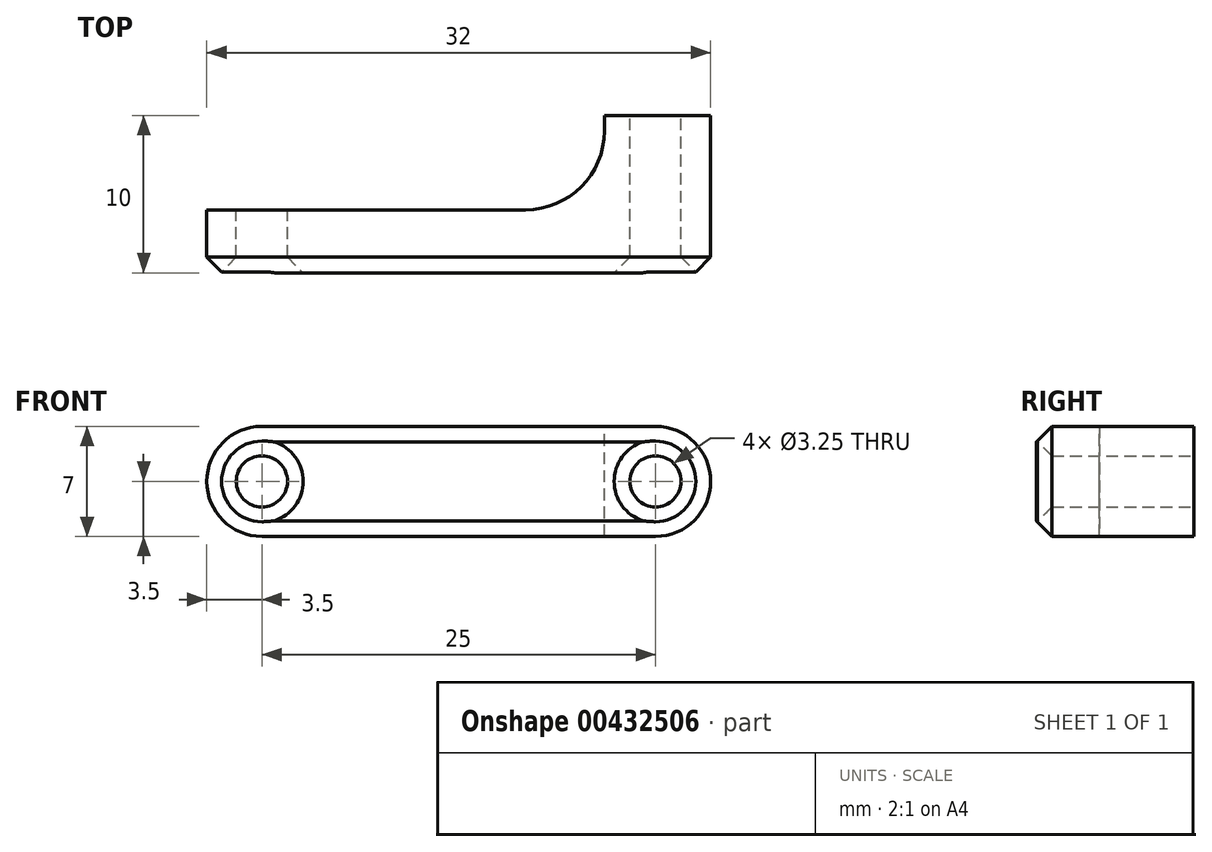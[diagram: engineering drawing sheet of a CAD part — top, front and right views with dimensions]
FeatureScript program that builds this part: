
annotation { "Feature Type Name" : "Feature", "Feature Type Description" : "" }
export const myFeature = defineFeature(function(context is Context, id is Id, definition is map)
    precondition{}
    {
        {
            var Q0;
            Q0=qCreatedBy(makeId("Front.planeOp"),FACE);
            var sketch = newSketch(context, id + "F0", { "sketchPlane" : qUnion([Q0])});
            skLineSegment(sketch, "E0", {"start": v(0, 0) * mm, "end": v(25, 0) * mm});
            skCircle(sketch, "E1", {"center": v(0, 0) * mm, "radius": 1.63 * mm});
            skCircle(sketch, "E2", {"center": v(25, 0) * mm, "radius": 1.63 * mm});
            skCircle(sketch, "E3", {"center": v(0, 0) * mm, "radius": 3.5 * mm});
            skCircle(sketch, "E4", {"center": v(25, 0) * mm, "radius": 3.5 * mm});
            skLineSegment(sketch, "E5", {"start": v(0, 3.5) * mm, "end": v(25, 3.5) * mm});
            skLineSegment(sketch, "E6", {"start": v(0, -3.5) * mm, "end": v(25, -3.5) * mm});
            skSolve(sketch);
        }
        {
            var Q0;
            Q0 = qSketchRegion(id + "F0", true);
            extrude(context, id + "F1", {"entities" : qUnion([Q0]), "depth" : 10 * mm});
        }
        {
            var Q0;
            Q0=makeQuery(id+"F1.opExtrude","SWEPT_FACE",FACE,{"disambiguationData":[OSD([sQuery(id+"F0.wireOp",EDGE,"E5")])]});
            var sketch = newSketch(context, id + "F2", { "sketchPlane" : qUnion([Q0])});
            skLineSegment(sketch, "E7", {"start": v(-13.96, 0) * mm, "end": v(40.07, 0) * mm});
            skLineSegment(sketch, "E8", {"start": v(-13.96, -6) * mm, "end": v(16.75, -6) * mm});
            skLineSegment(sketch, "E9", {"start": v(-3.6, 0) * mm, "end": v(-3.6, -10) * mm});
            skLineSegment(sketch, "E10", {"start": v(-3.6, -10) * mm, "end": v(35.1, -10) * mm});
            skLineSegment(sketch, "E11", {"start": v(0, 0) * mm, "end": v(0, -10) * mm});
            skLineSegment(sketch, "E12", {"start": v(15.75, 0) * mm, "end": v(15.75, -10) * mm});
            skLineSegment(sketch, "E13", {"start": v(-3.6, -4) * mm, "end": v(35.1, -4) * mm});
            skLineSegment(sketch, "E14", {"start": v(7.87, 0) * mm, "end": v(7.88, -10) * mm});
            skLineSegment(sketch, "E15", {"start": v(21.75, 0) * mm, "end": v(21.75, -1) * mm});
            skPoint(sketch, "E16.newPointB", {"position": v(40.07, -6) * mm});
            skArc(sketch, "E16.filletArc", {"start": v(16.75, -6) * mm, "mid": v(20.29, -4.54) * mm, "end": v(21.75, -1) * mm});
            skSolve(sketch);
        }
        {
            var Q0;
            {var subQ0=sQuery(id+"F2.wireOp",EDGE,"E11");var subQ1=sQuery(id+"F2.wireOp",EDGE,"E8");var subQ2=makeQuery(id+"F2.imprint","INTERSECT",VERTEX,{"derivedFrom":[subQ1,subQ0]});Q0=makeQuery(id+"F2.imprint","IMPRINT",FACE,{"disambiguationData":[TD([[makeQuery(id+"F2.imprint","IMPRINT",EDGE,{"disambiguationData":[TD([[subQ2,-1.0]])],"derivedFrom":subQ1}),1.0]])]});}
            var Q1;
            {var subQ0=sQuery(id+"F2.wireOp",EDGE,"E11");var subQ1=sQuery(id+"F2.wireOp",EDGE,"E7");var subQ2=makeQuery(id+"F2.imprint","INTERSECT",VERTEX,{"derivedFrom":[subQ1,subQ0]});Q1=makeQuery(id+"F2.imprint","IMPRINT",FACE,{"disambiguationData":[TD([[makeQuery(id+"F2.imprint","IMPRINT",EDGE,{"disambiguationData":[TD([[subQ2,-1.0]])],"derivedFrom":subQ1}),-1.0]])]});}
            var Q2;
            {var subQ0=sQuery(id+"F2.wireOp",EDGE,"E14");var subQ1=sQuery(id+"F2.wireOp",EDGE,"E8");var subQ2=makeQuery(id+"F2.imprint","INTERSECT",VERTEX,{"derivedFrom":[subQ1,subQ0]});Q2=makeQuery(id+"F2.imprint","IMPRINT",FACE,{"disambiguationData":[TD([[makeQuery(id+"F2.imprint","IMPRINT",EDGE,{"disambiguationData":[TD([[subQ2,-1.0]])],"derivedFrom":subQ1}),1.0]])]});}
            var Q3;
            {var subQ0=sQuery(id+"F2.wireOp",EDGE,"E11");var subQ1=sQuery(id+"F2.wireOp",EDGE,"E7");var subQ2=makeQuery(id+"F2.imprint","INTERSECT",VERTEX,{"derivedFrom":[subQ1,subQ0]});Q3=makeQuery(id+"F2.imprint","IMPRINT",FACE,{"disambiguationData":[TD([[makeQuery(id+"F2.imprint","IMPRINT",EDGE,{"disambiguationData":[TD([[subQ2,1.0]])],"derivedFrom":subQ1}),-1.0]])]});}
            var Q4;
            {var subQ0=sQuery(id+"F2.wireOp",EDGE,"E9");var subQ1=sQuery(id+"F2.wireOp",EDGE,"E8");var subQ2=makeQuery(id+"F2.imprint","INTERSECT",VERTEX,{"derivedFrom":[subQ1,subQ0]});Q4=makeQuery(id+"F2.imprint","IMPRINT",FACE,{"disambiguationData":[TD([[makeQuery(id+"F2.imprint","IMPRINT",EDGE,{"disambiguationData":[TD([[subQ2,-1.0]])],"derivedFrom":subQ1}),1.0]])]});}
            var Q5;
            {var subQ0=sQuery(id+"F2.wireOp",EDGE,"E12");var subQ1=sQuery(id+"F2.wireOp",EDGE,"E7");var subQ2=makeQuery(id+"F2.imprint","INTERSECT",VERTEX,{"derivedFrom":[subQ1,subQ0]});Q5=makeQuery(id+"F2.imprint","IMPRINT",FACE,{"disambiguationData":[TD([[makeQuery(id+"F2.imprint","IMPRINT",EDGE,{"disambiguationData":[TD([[subQ2,1.0]])],"derivedFrom":subQ1}),-1.0]])]});}
            var Q6;
            Q6=makeQuery(id+"F1.opExtrude","SWEPT_FACE",FACE,{"disambiguationData":[OSD([sQuery(id+"F0.wireOp",EDGE,"E6")])]});
            var Q7;
            {var subQ0=sQuery(id+"F2.wireOp",EDGE,"E12");var subQ1=sQuery(id+"F2.wireOp",EDGE,"E7");var subQ2=makeQuery(id+"F2.imprint","INTERSECT",VERTEX,{"derivedFrom":[subQ1,subQ0]});Q7=makeQuery(id+"F2.imprint","IMPRINT",FACE,{"disambiguationData":[TD([[makeQuery(id+"F2.imprint","IMPRINT",EDGE,{"disambiguationData":[TD([[subQ2,-1.0]])],"derivedFrom":subQ1}),-1.0]])]});}
            var Q8;
            {var subQ0=sQuery(id+"F2.wireOp",EDGE,"E12");var subQ1=sQuery(id+"F2.wireOp",EDGE,"E8");var subQ2=makeQuery(id+"F2.imprint","INTERSECT",VERTEX,{"derivedFrom":[subQ1,subQ0]});Q8=makeQuery(id+"F2.imprint","IMPRINT",FACE,{"disambiguationData":[TD([[makeQuery(id+"F2.imprint","IMPRINT",EDGE,{"disambiguationData":[TD([[subQ2,-1.0]])],"derivedFrom":subQ1}),1.0]])]});}
            extrude(context, id + "F3", {"entities" : qUnion([Q0, Q1, Q2, Q3, Q4, Q5, Q6, Q7, Q8]), "operationType" : NewBodyOperationType.REMOVE, "oppositeDirection" : true, "depth" : 25 * mm});
        }
        {
            var Q0;
            Q0=makeQuery(id+"F1.opExtrude","CAP_EDGE",EDGE,{"disambiguationData":[OSD([sQuery(id+"F0.wireOp",EDGE,"E5")])],"isStart":false});
            var Q1;
            Q1=makeQuery(id+"F1.opExtrude","CAP_FACE",FACE,{"disambiguationData":[OSD([sQuery(id+"F0.wireOp",EDGE,"E1"),sQuery(id+"F0.wireOp",EDGE,"E2"),sQuery(id+"F0.wireOp",EDGE,"E3"),sQuery(id+"F0.wireOp",EDGE,"E4"),sQuery(id+"F0.wireOp",EDGE,"E5"),sQuery(id+"F0.wireOp",EDGE,"E6")])],"isStart":false});
            chamfer(context, id + "F4", {"entities" : qUnion([Q0, Q1]), "width" : 1 * mm, "tangentPropagation" : true});
        }
    });
